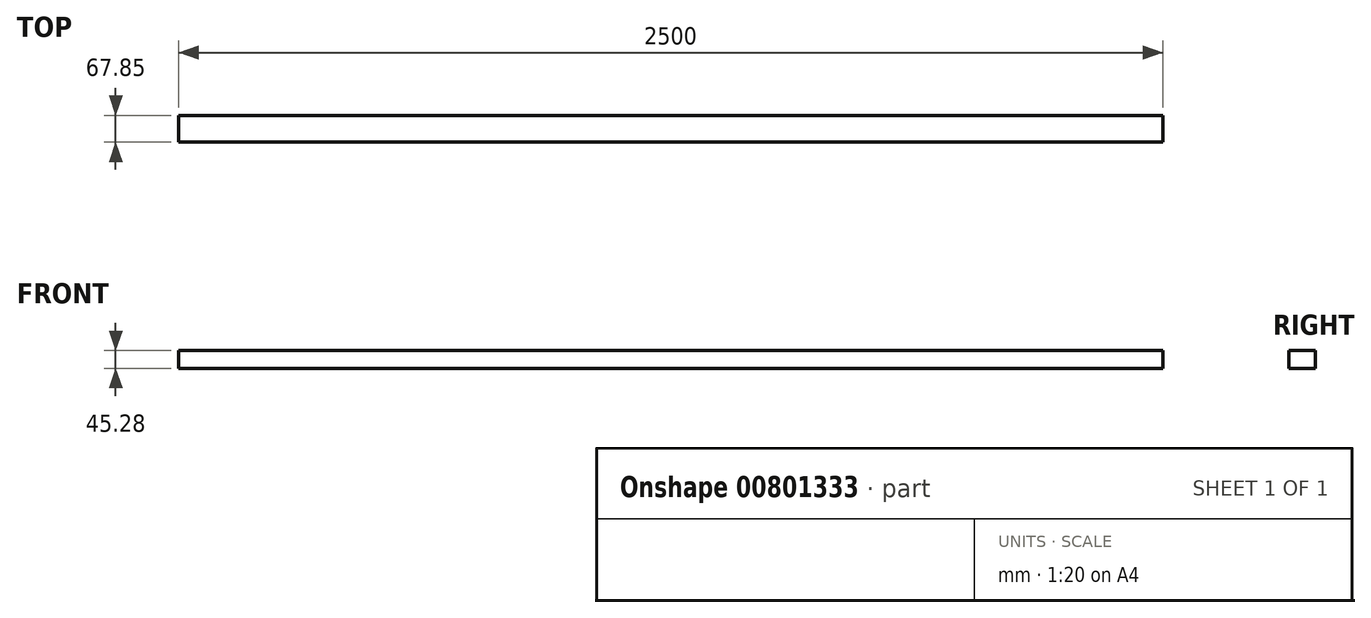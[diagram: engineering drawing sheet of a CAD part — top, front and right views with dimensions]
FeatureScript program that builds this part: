
annotation { "Feature Type Name" : "Feature", "Feature Type Description" : "" }
export const myFeature = defineFeature(function(context is Context, id is Id, definition is map)
    precondition{}
    {
        {
            var Q0;
            Q0=qCreatedBy(makeId("Right.planeOp"),FACE);
            var sketch = newSketch(context, id + "F0", { "sketchPlane" : qUnion([Q0])});
            skLineSegment(sketch, "E0.bottom", {"start": v(0, 0) * mm, "end": v(67.85, 0) * mm});
            skLineSegment(sketch, "E0.top", {"start": v(0, -45.28) * mm, "end": v(67.85, -45.28) * mm});
            skLineSegment(sketch, "E0.left", {"start": v(0, 0) * mm, "end": v(0, -45.28) * mm});
            skLineSegment(sketch, "E0.right", {"start": v(67.85, 0) * mm, "end": v(67.85, -45.28) * mm});
            skSolve(sketch);
        }
        {
            var Q0;
            Q0 = qSketchRegion(id + "F0", true);
            extrude(context, id + "F1", {"entities" : qUnion([Q0]), "depth" : 2500 * mm, "offsetDistance" : 25 * mm});
        }
    });
